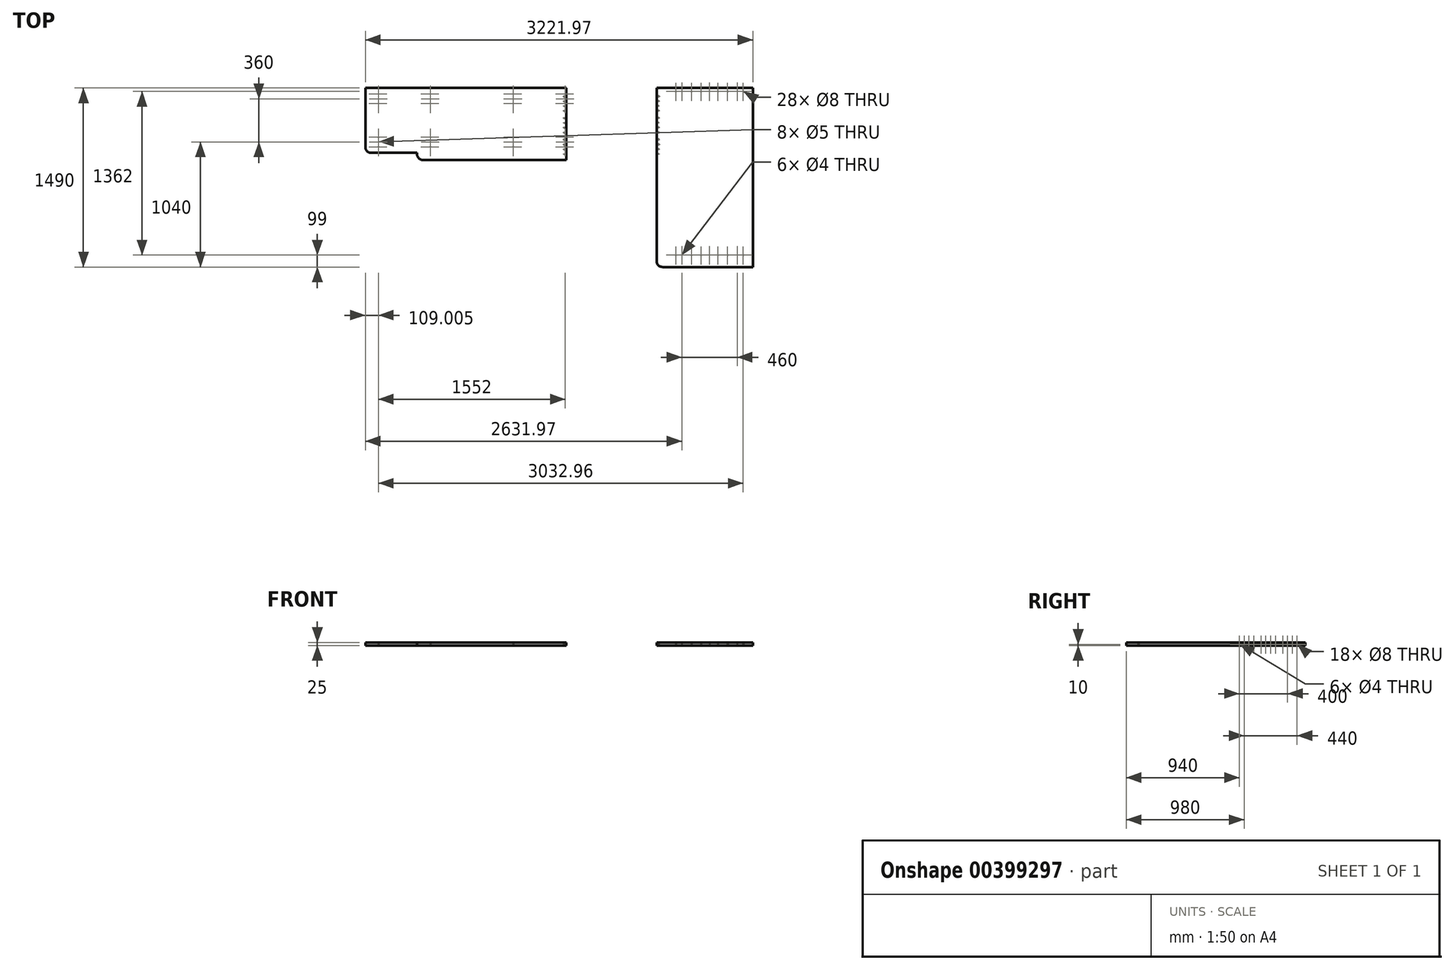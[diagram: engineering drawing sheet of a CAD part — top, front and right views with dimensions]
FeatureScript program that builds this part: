
annotation { "Feature Type Name" : "Feature", "Feature Type Description" : "" }
export const myFeature = defineFeature(function(context is Context, id is Id, definition is map)
    precondition{}
    {
        {
            var Q0;
            Q0=qCreatedBy(makeId("Top.planeOp"),FACE);
            var sketch = newSketch(context, id + "F0", { "sketchPlane" : qUnion([Q0])});
            skLineSegment(sketch, "E0.bottom", {"start": v(-2341.59, 0) * mm, "end": v(-671.59, 0) * mm});
            skLineSegment(sketch, "E0.left", {"start": v(-2341.59, 0) * mm, "end": v(-2341.59, -490) * mm});
            skLineSegment(sketch, "E0.right", {"start": v(-671.59, 0) * mm, "end": v(-671.59, -600) * mm});
            skLineSegment(sketch, "E1", {"start": v(-671.59, -600) * mm, "end": v(-1861.59, -600) * mm});
            skLineSegment(sketch, "E2", {"start": v(-2291.59, -540) * mm, "end": v(-1911.59, -540) * mm});
            skLineSegment(sketch, "E3", {"start": v(-1911.59, -540) * mm, "end": v(-1911.59, -550) * mm});
            skPoint(sketch, "E4.visualSharp", {"position": v(-2341.59, -540) * mm});
            skArc(sketch, "E4.filletArc", {"start": v(-2341.59, -490) * mm, "mid": v(-2326.94, -525.36) * mm, "end": v(-2291.59, -540) * mm});
            skPoint(sketch, "E5.visualSharp", {"position": v(-1911.59, -600) * mm});
            skArc(sketch, "E5.filletArc", {"start": v(-1911.59, -550) * mm, "mid": v(-1896.94, -585.36) * mm, "end": v(-1861.59, -600) * mm});
            skLineSegment(sketch, "E6", {"start": v(0, 0) * mm, "end": v(-671.59, 0) * mm, "construction": true});
            skSolve(sketch);
        }
        {
            var Q0;
            Q0=qCreatedBy(makeId("Top.planeOp"),FACE);
            var sketch = newSketch(context, id + "F1", { "sketchPlane" : qUnion([Q0])});
            skLineSegment(sketch, "E7.bottom", {"start": v(80.38, 0) * mm, "end": v(880.38, 0) * mm});
            skLineSegment(sketch, "E7.top", {"start": v(130.38, -1490) * mm, "end": v(880.38, -1490) * mm});
            skLineSegment(sketch, "E7.left", {"start": v(80.38, 0) * mm, "end": v(80.38, -1440) * mm});
            skLineSegment(sketch, "E7.right", {"start": v(880.38, 0) * mm, "end": v(880.38, -1490) * mm});
            skPoint(sketch, "E8.visualSharp", {"position": v(80.38, -1490) * mm});
            skArc(sketch, "E8.filletArc", {"start": v(80.38, -1440) * mm, "mid": v(95.02, -1475.36) * mm, "end": v(130.38, -1490) * mm});
            skLineSegment(sketch, "E9", {"start": v(0, 0) * mm, "end": v(80.38, 0) * mm, "construction": true});
            skSolve(sketch);
        }
        {
            var Q0;
            Q0=makeQuery(id+"F0.imprint","IMPRINT",FACE,{"disambiguationData":[TD([[makeQuery(id+"F0.imprint","IMPRINT",EDGE,{"derivedFrom":sQuery(id+"F0.wireOp",EDGE,"E0.bottom")}),-1.0]])]});
            extrude(context, id + "F2", {"entities" : qUnion([Q0]), "depth" : 25 * mm});
        }
        {
            var Q0;
            Q0=qSketchRegion(id+"F1",true);
            extrude(context, id + "F3", {"entities" : qUnion([Q0]), "depth" : 25 * mm});
        }
        {
            var Q0;
            Q0=makeQuery(id+"F2.opExtrude","CAP_FACE",FACE,{"disambiguationData":[OSD([sQuery(id+"F0.wireOp",EDGE,"E0.bottom"),sQuery(id+"F0.wireOp",EDGE,"E0.left"),sQuery(id+"F0.wireOp",EDGE,"E0.right"),sQuery(id+"F0.wireOp",EDGE,"E1"),sQuery(id+"F0.wireOp",EDGE,"E2"),sQuery(id+"F0.wireOp",EDGE,"E3"),sQuery(id+"F0.wireOp",EDGE,"E4.filletArc"),sQuery(id+"F0.wireOp",EDGE,"E5.filletArc")])],"isStart":true});
            var sketch = newSketch(context, id + "F4", { "sketchPlane" : qUnion([Q0])});
            skLineSegment(sketch, "E10", {"start": v(-680.59, 600) * mm, "end": v(-680.59, 0) * mm, "construction": true});
            skPoint(sketch, "E11", {"position": v(-680.59, 50) * mm});
            skPoint(sketch, "E12.0.1.0", {"position": v(-680.59, 90) * mm});
            skPoint(sketch, "E12.0.2.0", {"position": v(-680.59, 130) * mm});
            skPoint(sketch, "E12.1.0.0", {"position": v(-1112.59, 50) * mm});
            skPoint(sketch, "E12.1.1.0", {"position": v(-1112.59, 90) * mm});
            skPoint(sketch, "E12.1.2.0", {"position": v(-1112.59, 130) * mm});
            skLineSegment(sketch, "E12.direction1", {"start": v(-680.59, 50) * mm, "end": v(-1112.59, 50) * mm, "construction": true});
            skLineSegment(sketch, "E12.direction2", {"start": v(-680.59, 50) * mm, "end": v(-680.59, 90) * mm, "construction": true});
            skLineSegment(sketch, "E13.0.1.0", {"start": v(-680.59, 410) * mm, "end": v(-1112.59, 410) * mm, "construction": true});
            skLineSegment(sketch, "E13.0.1.1", {"start": v(-680.59, 410) * mm, "end": v(-680.59, 450) * mm, "construction": true});
            skPoint(sketch, "E13.0.1.2", {"position": v(-680.59, 410) * mm});
            skPoint(sketch, "E13.0.1.3", {"position": v(-680.59, 450) * mm});
            skPoint(sketch, "E13.0.1.4", {"position": v(-680.59, 490) * mm});
            skPoint(sketch, "E13.0.1.5", {"position": v(-1112.59, 410) * mm});
            skPoint(sketch, "E13.0.1.6", {"position": v(-1112.59, 450) * mm});
            skPoint(sketch, "E13.0.1.7", {"position": v(-1112.59, 490) * mm});
            skLineSegment(sketch, "E13.1.0.0", {"start": v(-1800.59, 50) * mm, "end": v(-2232.59, 50) * mm, "construction": true});
            skLineSegment(sketch, "E13.1.0.1", {"start": v(-1800.59, 50) * mm, "end": v(-1800.59, 90) * mm, "construction": true});
            skPoint(sketch, "E13.1.0.2", {"position": v(-1800.59, 50) * mm});
            skPoint(sketch, "E13.1.0.3", {"position": v(-1800.59, 90) * mm});
            skPoint(sketch, "E13.1.0.4", {"position": v(-1800.59, 130) * mm});
            skPoint(sketch, "E13.1.0.5", {"position": v(-2232.59, 50) * mm});
            skPoint(sketch, "E13.1.0.6", {"position": v(-2232.59, 90) * mm});
            skPoint(sketch, "E13.1.0.7", {"position": v(-2232.59, 130) * mm});
            skLineSegment(sketch, "E13.1.1.0", {"start": v(-1800.59, 410) * mm, "end": v(-2232.59, 410) * mm, "construction": true});
            skLineSegment(sketch, "E13.1.1.1", {"start": v(-1800.59, 410) * mm, "end": v(-1800.59, 450) * mm, "construction": true});
            skPoint(sketch, "E13.1.1.2", {"position": v(-1800.59, 410) * mm});
            skPoint(sketch, "E13.1.1.3", {"position": v(-1800.59, 450) * mm});
            skPoint(sketch, "E13.1.1.4", {"position": v(-1800.59, 490) * mm});
            skPoint(sketch, "E13.1.1.5", {"position": v(-2232.59, 410) * mm});
            skPoint(sketch, "E13.1.1.6", {"position": v(-2232.59, 450) * mm});
            skPoint(sketch, "E13.1.1.7", {"position": v(-2232.59, 490) * mm});
            skLineSegment(sketch, "E13.direction1", {"start": v(-1112.59, 50) * mm, "end": v(-2232.59, 50) * mm, "construction": true});
            skLineSegment(sketch, "E13.direction2", {"start": v(-1112.59, 50) * mm, "end": v(-1112.59, 410) * mm, "construction": true});
            skSolve(sketch);
        }
        {
            var Q0;
            Q0=sQuery(id+"F4.wireOp",VERTEX,"E13.1.1.7");
            var Q1;
            Q1=sQuery(id+"F4.wireOp",VERTEX,"E13.1.1.5");
            var Q2;
            Q2=sQuery(id+"F4.wireOp",VERTEX,"E13.1.1.4");
            var Q3;
            Q3=sQuery(id+"F4.wireOp",VERTEX,"E13.1.1.2");
            var Q4;
            Q4=sQuery(id+"F4.wireOp",VERTEX,"E13.1.0.4");
            var Q5;
            Q5=sQuery(id+"F4.wireOp",VERTEX,"E13.1.0.2");
            var Q6;
            Q6=sQuery(id+"F4.wireOp",VERTEX,"E13.1.0.5");
            var Q7;
            Q7=sQuery(id+"F4.wireOp",VERTEX,"E13.1.0.7");
            var Q8;
            Q8=sQuery(id+"F4.wireOp",VERTEX,"E13.0.1.7");
            var Q9;
            Q9=sQuery(id+"F4.wireOp",VERTEX,"E13.0.1.5");
            var Q10;
            Q10=sQuery(id+"F4.wireOp",VERTEX,"E12.1.2.0");
            var Q11;
            Q11=sQuery(id+"F4.wireOp",VERTEX,"E12.1.0.0");
            var Q12;
            Q12=sQuery(id+"F4.wireOp",VERTEX,"E11");
            var Q13;
            Q13=sQuery(id+"F4.wireOp",VERTEX,"E12.0.2.0");
            var Q14;
            Q14=sQuery(id+"F4.wireOp",VERTEX,"E13.0.1.2");
            var Q15;
            Q15=sQuery(id+"F4.wireOp",VERTEX,"E13.0.1.4");
            var Q16;
            Q16=makeQuery(id+"F2.opExtrude","SWEPT_BODY",BODY,{"disambiguationData":[OSD([sQuery(id+"F0.wireOp",EDGE,"E0.bottom"),sQuery(id+"F0.wireOp",EDGE,"E0.left"),sQuery(id+"F0.wireOp",EDGE,"E0.right"),sQuery(id+"F0.wireOp",EDGE,"E1"),sQuery(id+"F0.wireOp",EDGE,"E2"),sQuery(id+"F0.wireOp",EDGE,"E3"),sQuery(id+"F0.wireOp",EDGE,"E4.filletArc"),sQuery(id+"F0.wireOp",EDGE,"E5.filletArc")])]});
            hole(context, id + "F5", {"style" : HoleStyle.SIMPLE, "endStyle" : HoleEndStyle.BLIND, "holeDiameter" : 8 * mm, "holeDepth" : 15 * mm, "isTappedThrough" : true, "tappedDepth" : 12 * mm, "tapClearance" : 3, "startFromSketch" : true, "locations" : qUnion([Q0, Q1, Q2, Q3, Q4, Q5, Q6, Q7, Q8, Q9, Q10, Q11, Q12, Q13, Q14, Q15]), "scope" : qUnion([Q16])});
        }
        {
            var Q0;
            Q0=sQuery(id+"F4.wireOp",VERTEX,"E13.1.1.6");
            var Q1;
            Q1=sQuery(id+"F4.wireOp",VERTEX,"E13.1.1.3");
            var Q2;
            Q2=sQuery(id+"F4.wireOp",VERTEX,"E13.1.0.3");
            var Q3;
            Q3=sQuery(id+"F4.wireOp",VERTEX,"E13.1.0.6");
            var Q4;
            Q4=sQuery(id+"F4.wireOp",VERTEX,"E13.0.1.6");
            var Q5;
            Q5=sQuery(id+"F4.wireOp",VERTEX,"E13.0.1.3");
            var Q6;
            Q6=sQuery(id+"F4.wireOp",VERTEX,"E12.0.1.0");
            var Q7;
            Q7=sQuery(id+"F4.wireOp",VERTEX,"E12.1.1.0");
            var Q8;
            Q8=makeQuery(id+"F2.opExtrude","SWEPT_BODY",BODY,{"disambiguationData":[OSD([sQuery(id+"F0.wireOp",EDGE,"E0.bottom"),sQuery(id+"F0.wireOp",EDGE,"E0.left"),sQuery(id+"F0.wireOp",EDGE,"E0.right"),sQuery(id+"F0.wireOp",EDGE,"E1"),sQuery(id+"F0.wireOp",EDGE,"E2"),sQuery(id+"F0.wireOp",EDGE,"E3"),sQuery(id+"F0.wireOp",EDGE,"E4.filletArc"),sQuery(id+"F0.wireOp",EDGE,"E5.filletArc")])]});
            hole(context, id + "F6", {"style" : HoleStyle.SIMPLE, "endStyle" : HoleEndStyle.BLIND, "holeDiameter" : 5 * mm, "holeDepth" : 10 * mm, "isTappedThrough" : true, "tappedDepth" : 12 * mm, "tapClearance" : 3, "startFromSketch" : true, "locations" : qUnion([Q0, Q1, Q2, Q3, Q4, Q5, Q6, Q7]), "scope" : qUnion([Q8])});
        }
        {
            var Q0;
            Q0=makeQuery(id+"F2.opExtrude","SWEPT_FACE",FACE,{"disambiguationData":[OSD([sQuery(id+"F0.wireOp",EDGE,"E0.right")])]});
            var sketch = newSketch(context, id + "F7", { "sketchPlane" : qUnion([Q0])});
            skLineSegment(sketch, "E14.bottom", {"start": v(-600, 25) * mm, "end": v(0, 25) * mm});
            skLineSegment(sketch, "E14.top", {"start": v(-600, 0) * mm, "end": v(0, 0) * mm});
            skLineSegment(sketch, "E14.left", {"start": v(-600, 25) * mm, "end": v(-600, 0) * mm});
            skLineSegment(sketch, "E14.right", {"start": v(0, 25) * mm, "end": v(0, 0) * mm});
            skLineSegment(sketch, "E15", {"start": v(-600, 10) * mm, "end": v(0, 10) * mm, "construction": true});
            skPoint(sketch, "E16", {"position": v(-70, 10) * mm});
            skPoint(sketch, "E17.1.0.0", {"position": v(-110, 10) * mm});
            skPoint(sketch, "E17.2.0.0", {"position": v(-150, 10) * mm});
            skPoint(sketch, "E17.3.0.0", {"position": v(-190, 10) * mm});
            skLineSegment(sketch, "E17.direction1", {"start": v(-70, 10) * mm, "end": v(-110, 10) * mm, "construction": true});
            skLineSegment(sketch, "E18.1.0.0", {"start": v(-250, 10) * mm, "end": v(-290, 10) * mm, "construction": true});
            skPoint(sketch, "E18.1.0.1", {"position": v(-330, 10) * mm});
            skPoint(sketch, "E18.1.0.2", {"position": v(-250, 10) * mm});
            skPoint(sketch, "E18.1.0.3", {"position": v(-290, 10) * mm});
            skPoint(sketch, "E18.1.0.4", {"position": v(-370, 10) * mm});
            skLineSegment(sketch, "E18.direction1", {"start": v(-190, 10) * mm, "end": v(-370, 10) * mm, "construction": true});
            skLineSegment(sketch, "E19.0.2.0", {"start": v(-430, 10) * mm, "end": v(-470, 10) * mm, "construction": true});
            skPoint(sketch, "E19.3.2.0", {"position": v(-510, 10) * mm});
            skPoint(sketch, "E19.4.2.0", {"position": v(-430, 10) * mm});
            skPoint(sketch, "E19.5.2.0", {"position": v(-470, 10) * mm});
            skPoint(sketch, "E19.6.2.0", {"position": v(-550, 10) * mm});
            skSolve(sketch);
        }
        {
            var Q0;
            Q0=sQuery(id+"F7.wireOp",VERTEX,"E19.3.2.0");
            var Q1;
            Q1=sQuery(id+"F7.wireOp",VERTEX,"E19.5.2.0");
            var Q2;
            Q2=sQuery(id+"F7.wireOp",VERTEX,"E19.4.2.0");
            var Q3;
            Q3=sQuery(id+"F7.wireOp",VERTEX,"E18.1.0.4");
            var Q4;
            Q4=sQuery(id+"F7.wireOp",VERTEX,"E18.1.0.1");
            var Q5;
            Q5=sQuery(id+"F7.wireOp",VERTEX,"E18.1.0.2");
            var Q6;
            Q6=sQuery(id+"F7.wireOp",VERTEX,"E17.3.0.0");
            var Q7;
            Q7=sQuery(id+"F7.wireOp",VERTEX,"E17.1.0.0");
            var Q8;
            Q8=sQuery(id+"F7.wireOp",VERTEX,"E16");
            var Q9;
            Q9=makeQuery(id+"F2.opExtrude","SWEPT_BODY",BODY,{"disambiguationData":[OSD([sQuery(id+"F0.wireOp",EDGE,"E0.bottom"),sQuery(id+"F0.wireOp",EDGE,"E0.left"),sQuery(id+"F0.wireOp",EDGE,"E0.right"),sQuery(id+"F0.wireOp",EDGE,"E1"),sQuery(id+"F0.wireOp",EDGE,"E2"),sQuery(id+"F0.wireOp",EDGE,"E3"),sQuery(id+"F0.wireOp",EDGE,"E4.filletArc"),sQuery(id+"F0.wireOp",EDGE,"E5.filletArc")])]});
            hole(context, id + "F8", {"style" : HoleStyle.SIMPLE, "endStyle" : HoleEndStyle.BLIND, "holeDiameter" : 8 * mm, "holeDepth" : 20 * mm, "isTappedThrough" : true, "tappedDepth" : 12 * mm, "tapClearance" : 3, "startFromSketch" : true, "locations" : qUnion([Q0, Q1, Q2, Q3, Q4, Q5, Q6, Q7, Q8]), "scope" : qUnion([Q9])});
        }
        {
            var Q0;
            Q0=sQuery(id+"F7.wireOp",VERTEX,"E17.2.0.0");
            var Q1;
            Q1=sQuery(id+"F7.wireOp",VERTEX,"E18.1.0.3");
            var Q2;
            Q2=sQuery(id+"F7.wireOp",VERTEX,"E19.6.2.0");
            var Q3;
            Q3=makeQuery(id+"F2.opExtrude","SWEPT_BODY",BODY,{"disambiguationData":[OSD([sQuery(id+"F0.wireOp",EDGE,"E0.bottom"),sQuery(id+"F0.wireOp",EDGE,"E0.left"),sQuery(id+"F0.wireOp",EDGE,"E0.right"),sQuery(id+"F0.wireOp",EDGE,"E1"),sQuery(id+"F0.wireOp",EDGE,"E2"),sQuery(id+"F0.wireOp",EDGE,"E3"),sQuery(id+"F0.wireOp",EDGE,"E4.filletArc"),sQuery(id+"F0.wireOp",EDGE,"E5.filletArc")])]});
            hole(context, id + "F9", {"style" : HoleStyle.SIMPLE, "endStyle" : HoleEndStyle.BLIND, "holeDiameter" : 4 * mm, "holeDepth" : 20 * mm, "isTappedThrough" : true, "tappedDepth" : 12 * mm, "tapClearance" : 3, "startFromSketch" : true, "locations" : qUnion([Q0, Q1, Q2]), "scope" : qUnion([Q3])});
        }
        {
            var Q0;
            Q0=sQuery(id+"F7.wireOp",VERTEX,"E19.3.2.0");
            var Q1;
            Q1=sQuery(id+"F7.wireOp",VERTEX,"E19.5.2.0");
            var Q2;
            Q2=sQuery(id+"F7.wireOp",VERTEX,"E19.4.2.0");
            var Q3;
            Q3=sQuery(id+"F7.wireOp",VERTEX,"E18.1.0.4");
            var Q4;
            Q4=sQuery(id+"F7.wireOp",VERTEX,"E18.1.0.1");
            var Q5;
            Q5=sQuery(id+"F7.wireOp",VERTEX,"E18.1.0.0.start");
            var Q6;
            Q6=sQuery(id+"F7.wireOp",VERTEX,"E17.3.0.0");
            var Q7;
            Q7=sQuery(id+"F7.wireOp",VERTEX,"E17.1.0.0");
            var Q8;
            Q8=sQuery(id+"F7.wireOp",VERTEX,"E16");
            var Q9;
            Q9=makeQuery(id+"F3.opExtrude","SWEPT_BODY",BODY,{"disambiguationData":[OSD([sQuery(id+"F1.wireOp",EDGE,"E7.bottom"),sQuery(id+"F1.wireOp",EDGE,"E7.top"),sQuery(id+"F1.wireOp",EDGE,"E7.left"),sQuery(id+"F1.wireOp",EDGE,"E7.right"),sQuery(id+"F1.wireOp",EDGE,"E8.filletArc")])]});
            hole(context, id + "F10", {"style" : HoleStyle.SIMPLE, "endStyle" : HoleEndStyle.BLIND, "oppositeDirection" : true, "holeDiameter" : 8 * mm, "holeDepth" : 20 * mm, "isTappedThrough" : true, "tappedDepth" : 12 * mm, "tapClearance" : 3, "locations" : qUnion([Q0, Q1, Q2, Q3, Q4, Q5, Q6, Q7, Q8]), "scope" : qUnion([Q9])});
        }
        {
            var Q0;
            Q0=sQuery(id+"F7.wireOp",VERTEX,"E18.1.0.3");
            var Q1;
            Q1=sQuery(id+"F7.wireOp",VERTEX,"E17.2.0.0");
            var Q2;
            Q2=sQuery(id+"F7.wireOp",VERTEX,"E19.6.2.0");
            var Q3;
            Q3=makeQuery(id+"F3.opExtrude","SWEPT_BODY",BODY,{"disambiguationData":[OSD([sQuery(id+"F1.wireOp",EDGE,"E7.bottom"),sQuery(id+"F1.wireOp",EDGE,"E7.top"),sQuery(id+"F1.wireOp",EDGE,"E7.left"),sQuery(id+"F1.wireOp",EDGE,"E7.right"),sQuery(id+"F1.wireOp",EDGE,"E8.filletArc")])]});
            hole(context, id + "F11", {"style" : HoleStyle.SIMPLE, "endStyle" : HoleEndStyle.BLIND, "oppositeDirection" : true, "holeDiameter" : 4 * mm, "holeDepth" : 20 * mm, "isTappedThrough" : true, "tappedDepth" : 12 * mm, "tapClearance" : 3, "locations" : qUnion([Q0, Q1, Q2]), "scope" : qUnion([Q3])});
        }
        {
            var Q0;
            Q0=makeQuery(id+"F1.imprint","IMPRINT",FACE,{"disambiguationData":[TD([[makeQuery(id+"F1.imprint","IMPRINT",EDGE,{"derivedFrom":sQuery(id+"F1.wireOp",EDGE,"E7.bottom")}),-1.0]])]});
            var sketch = newSketch(context, id + "F12", { "sketchPlane" : qUnion([Q0])});
            skLineSegment(sketch, "E20", {"start": v(80.38, -1391) * mm, "end": v(880.38, -1391) * mm, "construction": true});
            skPoint(sketch, "E21", {"position": v(800.38, -1391) * mm});
            skPoint(sketch, "E22", {"position": v(750.38, -1391) * mm});
            skPoint(sketch, "E23", {"position": v(670.38, -1391) * mm});
            skPoint(sketch, "E24", {"position": v(520.38, -1391) * mm});
            skPoint(sketch, "E25", {"position": v(590.38, -1391) * mm});
            skLineSegment(sketch, "E26", {"start": v(520.38, -1469.86) * mm, "end": v(520.38, -1312.14) * mm, "construction": true});
            skPoint(sketch, "E27.MirrorP", {"position": v(450.38, -1391) * mm});
            skPoint(sketch, "E28.MirrorP", {"position": v(370.38, -1391) * mm});
            skPoint(sketch, "E29.MirrorP", {"position": v(290.38, -1391) * mm});
            skPoint(sketch, "E30.MirrorP", {"position": v(240.38, -1391) * mm});
            skLineSegment(sketch, "E31", {"start": v(-56.04, -710) * mm, "end": v(972.9, -710) * mm, "construction": true});
            skLineSegment(sketch, "E32", {"start": v(-112.91, -29) * mm, "end": v(989.87, -29) * mm, "construction": true});
            skPoint(sketch, "E33.MirrorP", {"position": v(240.38, -29) * mm});
            skPoint(sketch, "E34.MirrorP", {"position": v(290.38, -29) * mm});
            skPoint(sketch, "E35.MirrorP", {"position": v(370.38, -29) * mm});
            skPoint(sketch, "E36.MirrorP", {"position": v(450.38, -29) * mm});
            skPoint(sketch, "E37.MirrorP", {"position": v(520.38, -29) * mm});
            skPoint(sketch, "E38.MirrorP", {"position": v(590.38, -29) * mm});
            skPoint(sketch, "E39.MirrorP", {"position": v(670.38, -29) * mm});
            skPoint(sketch, "E40.MirrorP", {"position": v(800.38, -29) * mm});
            skPoint(sketch, "E41.MirrorP", {"position": v(750.38, -29) * mm});
            skSolve(sketch);
        }
        {
            var Q0;
            Q0=sQuery(id+"F12.wireOp",VERTEX,"E22");
            var Q1;
            Q1=sQuery(id+"F12.wireOp",VERTEX,"E24");
            var Q2;
            Q2=sQuery(id+"F12.wireOp",VERTEX,"E29.MirrorP");
            var Q3;
            Q3=sQuery(id+"F12.wireOp",VERTEX,"E34.MirrorP");
            var Q4;
            Q4=sQuery(id+"F12.wireOp",VERTEX,"E37.MirrorP");
            var Q5;
            Q5=sQuery(id+"F12.wireOp",VERTEX,"E41.MirrorP");
            var Q6;
            Q6=makeQuery(id+"F3.opExtrude","SWEPT_BODY",BODY,{"disambiguationData":[OSD([sQuery(id+"F1.wireOp",EDGE,"E7.bottom"),sQuery(id+"F1.wireOp",EDGE,"E7.top"),sQuery(id+"F1.wireOp",EDGE,"E7.left"),sQuery(id+"F1.wireOp",EDGE,"E7.right"),sQuery(id+"F1.wireOp",EDGE,"E8.filletArc")])]});
            hole(context, id + "F13", {"style" : HoleStyle.SIMPLE, "endStyle" : HoleEndStyle.BLIND, "oppositeDirection" : true, "holeDiameter" : 4 * mm, "holeDepth" : 20 * mm, "isTappedThrough" : true, "tappedDepth" : 12 * mm, "tapClearance" : 3, "locations" : qUnion([Q0, Q1, Q2, Q3, Q4, Q5]), "scope" : qUnion([Q6])});
        }
        {
            var Q0;
            Q0=sQuery(id+"F12.wireOp",VERTEX,"E21");
            var Q1;
            Q1=sQuery(id+"F12.wireOp",VERTEX,"E23");
            var Q2;
            Q2=sQuery(id+"F12.wireOp",VERTEX,"E25");
            var Q3;
            Q3=sQuery(id+"F12.wireOp",VERTEX,"E27.MirrorP");
            var Q4;
            Q4=sQuery(id+"F12.wireOp",VERTEX,"E28.MirrorP");
            var Q5;
            Q5=sQuery(id+"F12.wireOp",VERTEX,"E30.MirrorP");
            var Q6;
            Q6=sQuery(id+"F12.wireOp",VERTEX,"E33.MirrorP");
            var Q7;
            Q7=sQuery(id+"F12.wireOp",VERTEX,"E35.MirrorP");
            var Q8;
            Q8=sQuery(id+"F12.wireOp",VERTEX,"E36.MirrorP");
            var Q9;
            Q9=sQuery(id+"F12.wireOp",VERTEX,"E38.MirrorP");
            var Q10;
            Q10=sQuery(id+"F12.wireOp",VERTEX,"E39.MirrorP");
            var Q11;
            Q11=sQuery(id+"F12.wireOp",VERTEX,"E40.MirrorP");
            var Q12;
            Q12=makeQuery(id+"F3.opExtrude","SWEPT_BODY",BODY,{"disambiguationData":[OSD([sQuery(id+"F1.wireOp",EDGE,"E7.bottom"),sQuery(id+"F1.wireOp",EDGE,"E7.top"),sQuery(id+"F1.wireOp",EDGE,"E7.left"),sQuery(id+"F1.wireOp",EDGE,"E7.right"),sQuery(id+"F1.wireOp",EDGE,"E8.filletArc")])]});
            hole(context, id + "F14", {"style" : HoleStyle.SIMPLE, "endStyle" : HoleEndStyle.BLIND, "oppositeDirection" : true, "holeDiameter" : 8 * mm, "holeDepth" : 20 * mm, "isTappedThrough" : true, "tappedDepth" : 12 * mm, "tapClearance" : 3, "locations" : qUnion([Q0, Q1, Q2, Q3, Q4, Q5, Q6, Q7, Q8, Q9, Q10, Q11]), "scope" : qUnion([Q12])});
        }
    });
